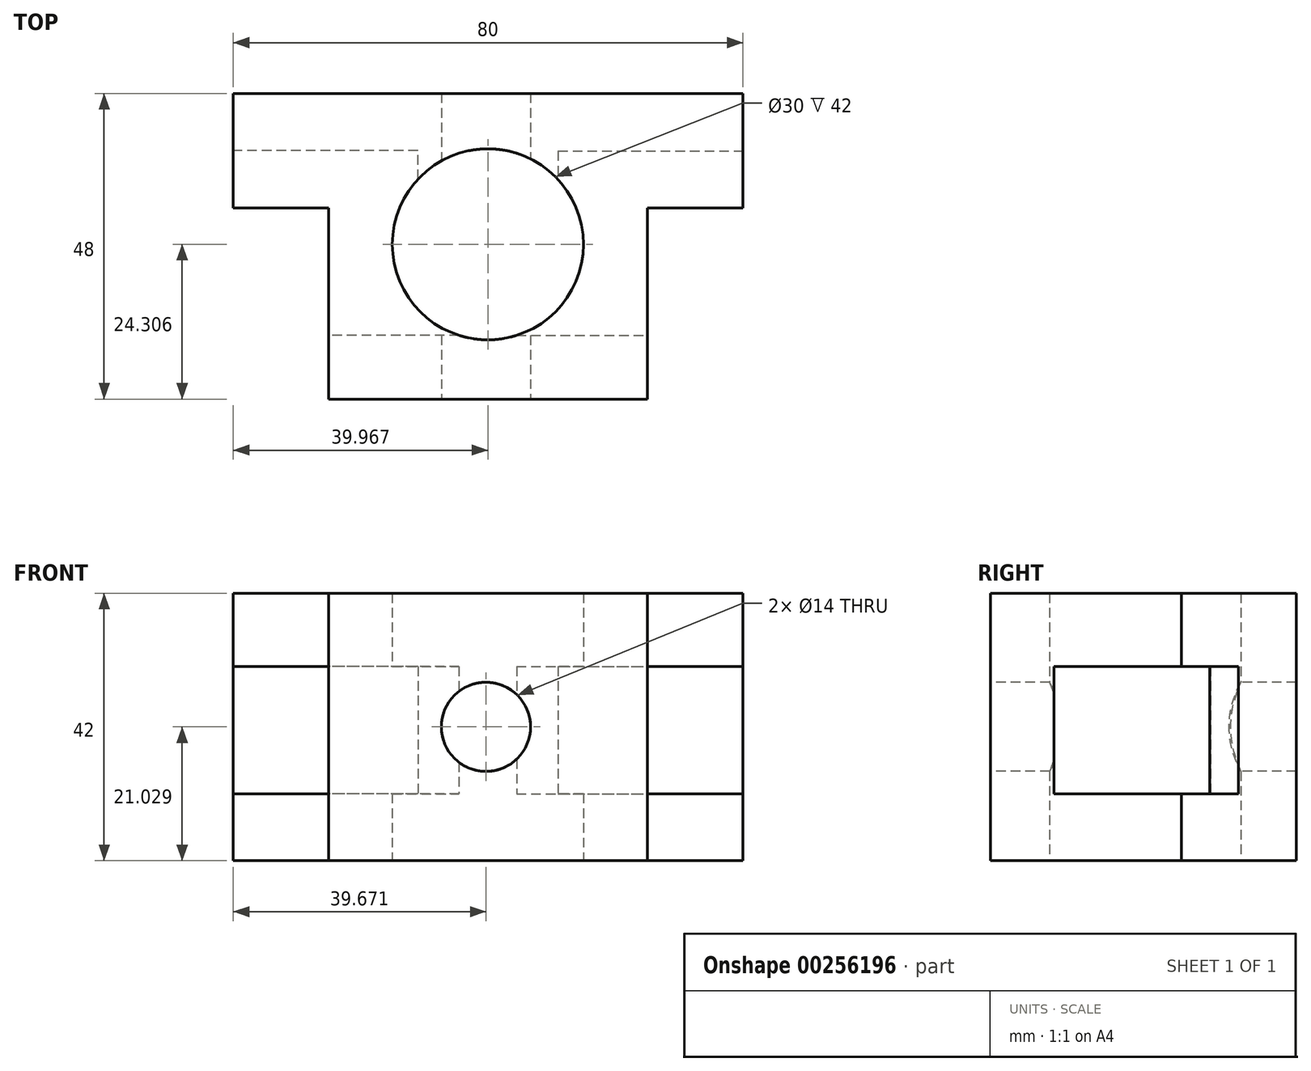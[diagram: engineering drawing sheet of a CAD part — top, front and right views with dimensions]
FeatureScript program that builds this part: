
annotation { "Feature Type Name" : "Feature", "Feature Type Description" : "" }
export const myFeature = defineFeature(function(context is Context, id is Id, definition is map)
    precondition{}
    {
        {
            var Q0;
            Q0=qCreatedBy(makeId("Front.planeOp"),FACE);
            var sketch = newSketch(context, id + "F0", { "sketchPlane" : qUnion([Q0])});
            skLineSegment(sketch, "E0.bottom", {"start": v(-45.74, -15.7) * mm, "end": v(34.26, -15.7) * mm});
            skLineSegment(sketch, "E0.top", {"start": v(-45.74, 26.3) * mm, "end": v(34.26, 26.3) * mm});
            skLineSegment(sketch, "E0.left", {"start": v(-45.74, -15.7) * mm, "end": v(-45.74, 26.3) * mm});
            skLineSegment(sketch, "E0.right", {"start": v(34.26, -15.7) * mm, "end": v(34.26, 26.3) * mm});
            skSolve(sketch);
        }
        {
            var Q0;
            Q0=makeQuery(id+"F0.imprint","IMPRINT",FACE,{"disambiguationData":[TD([[makeQuery(id+"F0.imprint","IMPRINT",EDGE,{"derivedFrom":sQuery(id+"F0.wireOp",EDGE,"E0.bottom")}),1.0]])]});
            extrude(context, id + "F1", {"entities" : qUnion([Q0]), "depth" : 18 * mm});
        }
        {
            var Q0;
            Q0=makeQuery(id+"F1.opExtrude","CAP_FACE",FACE,{"disambiguationData":[OSD([sQuery(id+"F0.wireOp",EDGE,"E0.bottom"),sQuery(id+"F0.wireOp",EDGE,"E0.top"),sQuery(id+"F0.wireOp",EDGE,"E0.left"),sQuery(id+"F0.wireOp",EDGE,"E0.right")])],"isStart":false});
            var sketch = newSketch(context, id + "F2", { "sketchPlane" : qUnion([Q0])});
            skLineSegment(sketch, "E1", {"start": v(-45.74, 26.3) * mm, "end": v(-30.74, 26.3) * mm});
            skLineSegment(sketch, "E2", {"start": v(-30.74, 26.3) * mm, "end": v(19.26, 26.3) * mm});
            skLineSegment(sketch, "E3", {"start": v(19.26, 26.3) * mm, "end": v(34.26, 26.3) * mm});
            skLineSegment(sketch, "E4", {"start": v(34.26, 26.3) * mm, "end": v(19.26, 26.3) * mm});
            skLineSegment(sketch, "E5", {"start": v(19.26, -15.7) * mm, "end": v(19.26, 26.3) * mm});
            skLineSegment(sketch, "E6", {"start": v(-30.74, 26.3) * mm, "end": v(-30.74, -15.7) * mm});
            skSolve(sketch);
        }
        {
            var Q0;
            Q0=makeQuery(id+"F2.imprint","IMPRINT",FACE,{"disambiguationData":[TD([[makeQuery(id+"F2.imprint","IMPRINT",EDGE,{"derivedFrom":sQuery(id+"F2.wireOp",EDGE,"E2")}),-1.0]])]});
            extrude(context, id + "F3", {"entities" : qUnion([Q0]), "operationType" : NewBodyOperationType.ADD, "depth" : 30 * mm});
        }
        {
            var Q0;
            Q0=makeQuery(id+"F3.opExtrude","CAP_FACE",FACE,{"disambiguationData":[OSD([sQuery(id+"F0.wireOp",EDGE,"E0.bottom"),sQuery(id+"F2.wireOp",EDGE,"E2"),sQuery(id+"F2.wireOp",EDGE,"E5"),sQuery(id+"F2.wireOp",EDGE,"E6")])],"isStart":false});
            var sketch = newSketch(context, id + "F4", { "sketchPlane" : qUnion([Q0])});
            skCircle(sketch, "E7", {"center": v(-6.07, 5.34) * mm, "radius": 7 * mm});
            skSolve(sketch);
        }
        {
            var Q0;
            Q0=makeQuery(id+"F4.imprint","IMPRINT",FACE,{"disambiguationData":[TD([[makeQuery(id+"F4.imprint","IMPRINT",EDGE,{"derivedFrom":sQuery(id+"F4.wireOp",EDGE,"E7")}),1.0]])]});
            extrude(context, id + "F5", {"entities" : qUnion([Q0]), "operationType" : NewBodyOperationType.REMOVE, "oppositeDirection" : true, "depth" : 48 * mm});
        }
        {
            var Q0;
            {var subQ0=sQuery(id+"F0.wireOp",EDGE,"E0.bottom");Q0=makeQuery(id+"F3.boolean.opBoolean","MERGE",FACE,{"derivedFrom":[makeQuery(id+"F1.opExtrude","SWEPT_FACE",FACE,{"disambiguationData":[OSD([subQ0])]}),makeQuery(id+"F3.opExtrude","SWEPT_FACE",FACE,{"disambiguationData":[OSD([subQ0])]})]});}
            var sketch = newSketch(context, id + "F6", { "sketchPlane" : qUnion([Q0])});
            skCircle(sketch, "E8", {"center": v(-5.77, 23.7) * mm, "radius": 15 * mm});
            skSolve(sketch);
        }
        {
            var Q0;
            Q0 = qSketchRegion(id + "F6", true);
            extrude(context, id + "F7", {"entities" : qUnion([Q0]), "operationType" : NewBodyOperationType.REMOVE, "oppositeDirection" : true, "depth" : 42 * mm});
        }
        {
            var Q0;
            Q0=makeQuery(id+"F1.opExtrude","SWEPT_FACE",FACE,{"disambiguationData":[OSD([sQuery(id+"F0.wireOp",EDGE,"E0.right")])]});
            var sketch = newSketch(context, id + "F8", { "sketchPlane" : qUnion([Q0])});
            skLineSegment(sketch, "E9", {"start": v(0, -15.7) * mm, "end": v(0, -4.7) * mm});
            skLineSegment(sketch, "E10", {"start": v(0, -4.7) * mm, "end": v(0, 15.3) * mm});
            skLineSegment(sketch, "E11", {"start": v(0, 15.3) * mm, "end": v(0, 26.3) * mm});
            skLineSegment(sketch, "E12", {"start": v(-18, -15.7) * mm, "end": v(-9, -15.7) * mm});
            skLineSegment(sketch, "E13", {"start": v(-9, -15.7) * mm, "end": v(-9, 26.3) * mm});
            skLineSegment(sketch, "E14", {"start": v(-9, 26.3) * mm, "end": v(-18, 26.3) * mm});
            skSolve(sketch);
        }
        {
            var Q0;
            Q0=makeQuery(id+"F8.imprint","IMPRINT",FACE,{"disambiguationData":[TD([[makeQuery(id+"F8.imprint","IMPRINT",EDGE,{"derivedFrom":sQuery(id+"F8.wireOp",EDGE,"E12")}),1.0]])]});
            var sketch = newSketch(context, id + "F9", { "sketchPlane" : qUnion([Q0])});
            skLineSegment(sketch, "E15.bottom", {"start": v(-9.06, -5.18) * mm, "end": v(-18.06, -5.18) * mm});
            skLineSegment(sketch, "E15.top", {"start": v(-9.06, 14.82) * mm, "end": v(-18.06, 14.82) * mm});
            skLineSegment(sketch, "E15.left", {"start": v(-9.06, -5.18) * mm, "end": v(-9.06, 14.82) * mm});
            skLineSegment(sketch, "E15.right", {"start": v(-18.06, -5.18) * mm, "end": v(-18.06, 14.82) * mm});
            skSolve(sketch);
        }
        {
            var Q0;
            {var subQ0=sQuery(id+"F9.wireOp",EDGE,"E15.left");Q0=makeQuery(id+"F9.imprint","IMPRINT",FACE,{"disambiguationData":[TD([[makeQuery(id+"F9.imprint","IMPRINT",EDGE,{"derivedFrom":subQ0}),1.0]])]});}
            extrude(context, id + "F10", {"entities" : qUnion([Q0]), "operationType" : NewBodyOperationType.REMOVE, "oppositeDirection" : true, "depth" : 29 * mm});
        }
        {
            var Q0;
            Q0=makeQuery(id+"F3.opExtrude","SWEPT_FACE",FACE,{"disambiguationData":[OSD([sQuery(id+"F2.wireOp",EDGE,"E5")])]});
            var sketch = newSketch(context, id + "F11", { "sketchPlane" : qUnion([Q0])});
            skLineSegment(sketch, "E16", {"start": v(-18, -5.18) * mm, "end": v(-38, -5.18) * mm});
            skLineSegment(sketch, "E17", {"start": v(-38, -5.18) * mm, "end": v(-38, 14.82) * mm});
            skLineSegment(sketch, "E18", {"start": v(-38, 14.82) * mm, "end": v(-18, 14.82) * mm});
            skSolve(sketch);
        }
        {
            var Q0;
            Q0=makeQuery(id+"F11.imprint","IMPRINT",FACE,{"disambiguationData":[TD([[makeQuery(id+"F11.imprint","IMPRINT",EDGE,{"derivedFrom":sQuery(id+"F11.wireOp",EDGE,"E16")}),-1.0]])]});
            extrude(context, id + "F12", {"entities" : qUnion([Q0]), "operationType" : NewBodyOperationType.REMOVE, "oppositeDirection" : true, "depth" : 29 * mm});
        }
        {
            var Q0;
            Q0=makeQuery(id+"F3.opExtrude","SWEPT_FACE",FACE,{"disambiguationData":[OSD([sQuery(id+"F2.wireOp",EDGE,"E6")])]});
            var sketch = newSketch(context, id + "F13", { "sketchPlane" : qUnion([Q0])});
            skLineSegment(sketch, "E19.bottom", {"start": v(38, 14.82) * mm, "end": v(18, 14.82) * mm});
            skLineSegment(sketch, "E19.top", {"start": v(38, -5.18) * mm, "end": v(18, -5.18) * mm});
            skLineSegment(sketch, "E19.left", {"start": v(38, 14.82) * mm, "end": v(38, -5.18) * mm});
            skLineSegment(sketch, "E19.right", {"start": v(18, 14.82) * mm, "end": v(18, -5.18) * mm});
            skSolve(sketch);
        }
        {
            var Q0;
            Q0=makeQuery(id+"F13.imprint","IMPRINT",FACE,{"disambiguationData":[TD([[makeQuery(id+"F13.imprint","IMPRINT",EDGE,{"derivedFrom":sQuery(id+"F13.wireOp",EDGE,"E19.bottom")}),1.0]])]});
            extrude(context, id + "F14", {"entities" : qUnion([Q0]), "operationType" : NewBodyOperationType.REMOVE, "oppositeDirection" : true, "depth" : 29 * mm});
        }
        {
            var Q0;
            Q0=makeQuery(id+"F1.opExtrude","SWEPT_FACE",FACE,{"disambiguationData":[OSD([sQuery(id+"F0.wireOp",EDGE,"E0.left")])]});
            var sketch = newSketch(context, id + "F15", { "sketchPlane" : qUnion([Q0])});
            skLineSegment(sketch, "E20.bottom", {"start": v(18, 14.82) * mm, "end": v(9, 14.82) * mm});
            skLineSegment(sketch, "E20.top", {"start": v(18, -5.18) * mm, "end": v(9, -5.18) * mm});
            skLineSegment(sketch, "E20.left", {"start": v(18, 14.82) * mm, "end": v(18, -5.18) * mm});
            skLineSegment(sketch, "E20.right", {"start": v(9, 14.82) * mm, "end": v(9, -5.18) * mm});
            skSolve(sketch);
        }
        {
            var Q0;
            Q0=makeQuery(id+"F15.imprint","IMPRINT",FACE,{"disambiguationData":[TD([[makeQuery(id+"F15.imprint","IMPRINT",EDGE,{"derivedFrom":sQuery(id+"F15.wireOp",EDGE,"E20.bottom")}),1.0]])]});
            extrude(context, id + "F16", {"entities" : qUnion([Q0]), "operationType" : NewBodyOperationType.REMOVE, "oppositeDirection" : true, "depth" : 29 * mm});
        }
    });
